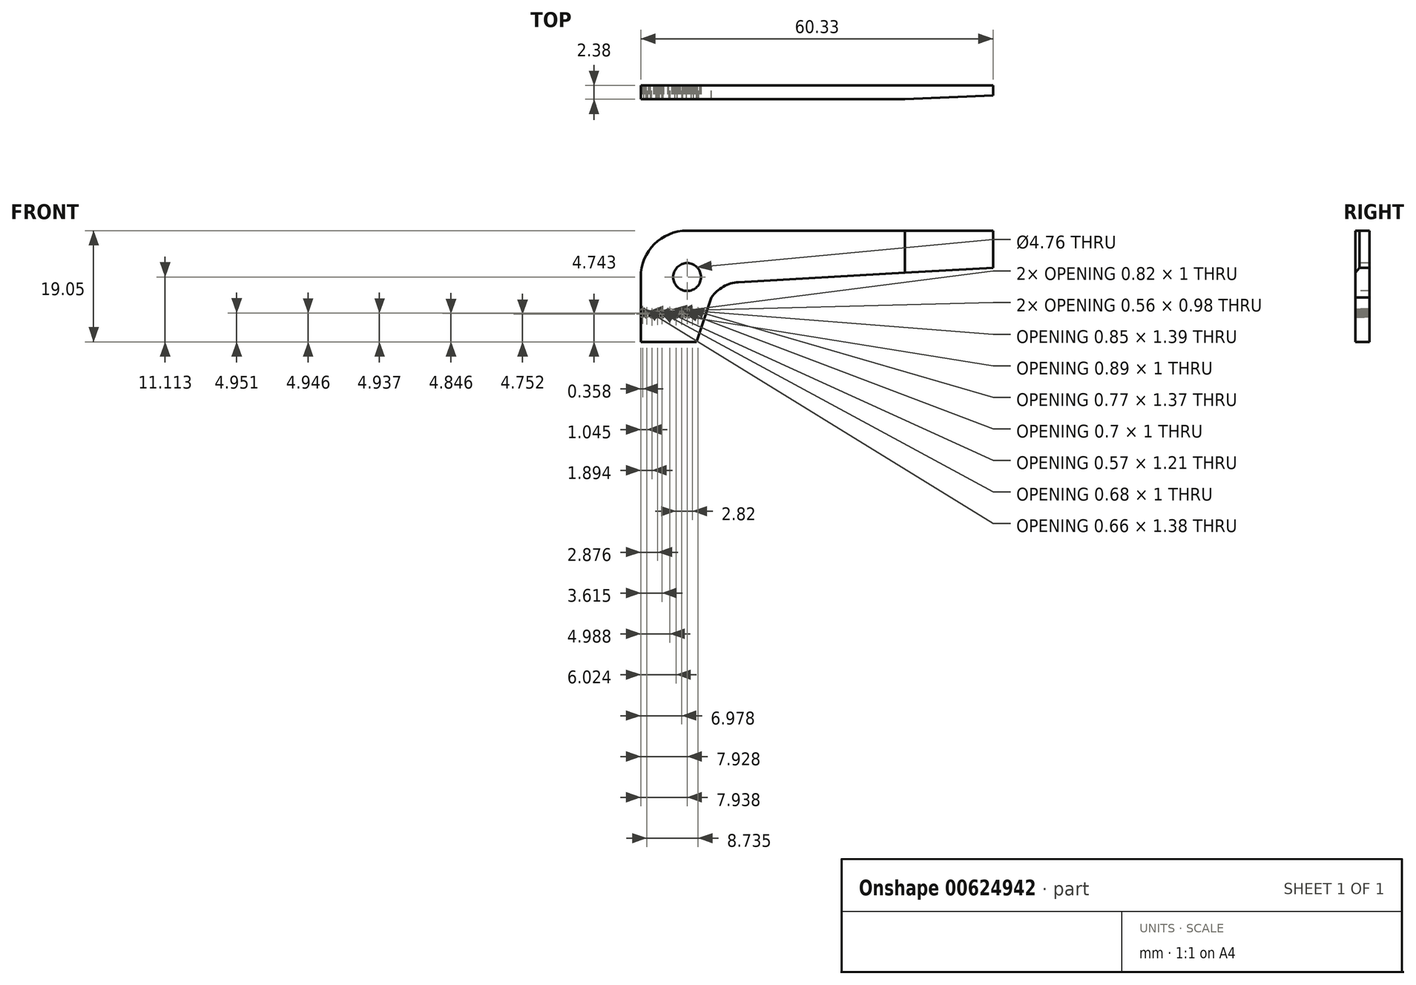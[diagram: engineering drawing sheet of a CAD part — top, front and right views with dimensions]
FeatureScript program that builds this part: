
annotation { "Feature Type Name" : "Feature", "Feature Type Description" : "" }
export const myFeature = defineFeature(function(context is Context, id is Id, definition is map)
    precondition{}
    {
        {
            var Q0;
            Q0=qCreatedBy(makeId("Front.planeOp"),FACE);
            var sketch = newSketch(context, id + "F0", { "sketchPlane" : qUnion([Q0])});
            skLineSegment(sketch, "E0.top", {"start": v(7.94, 19.05) * mm, "end": v(60.33, 19.05) * mm});
            skLineSegment(sketch, "E0.left", {"start": v(0, 0) * mm, "end": v(0, 11.11) * mm});
            skLineSegment(sketch, "E1", {"start": v(9.53, 0) * mm, "end": v(12.11, 7.63) * mm});
            skLineSegment(sketch, "E2", {"start": v(60.33, 12.7) * mm, "end": v(16.75, 10.23) * mm});
            skLineSegment(sketch, "E3", {"start": v(9.53, 0) * mm, "end": v(0, 0) * mm});
            skLineSegment(sketch, "E4", {"start": v(60.33, 12.7) * mm, "end": v(60.33, 19.05) * mm});
            skArc(sketch, "E5", {"start": v(16.75, 10.23) * mm, "mid": v(14.13, 9.46) * mm, "end": v(12.11, 7.63) * mm});
            skPoint(sketch, "E6.visualSharp", {"position": v(0, 19.05) * mm});
            skArc(sketch, "E6.filletArc", {"start": v(7.94, 19.05) * mm, "mid": v(2.32, 16.73) * mm, "end": v(0, 11.11) * mm});
            skSolve(sketch);
        }
        {
            var Q0;
            Q0 = qSketchRegion(id + "F0", true);
            extrude(context, id + "F1", {"entities" : qUnion([Q0]), "depth" : 2.38 * mm, "offsetDistance" : 25.4 * mm});
        }
        {
            var Q0;
            Q0=makeQuery(id+"F1.opExtrude","CAP_FACE",FACE,{"disambiguationData":[OSD([sQuery(id+"F0.wireOp",EDGE,"E0.top"),sQuery(id+"F0.wireOp",EDGE,"E0.left"),sQuery(id+"F0.wireOp",EDGE,"E1"),sQuery(id+"F0.wireOp",EDGE,"E2"),sQuery(id+"F0.wireOp",EDGE,"E3"),sQuery(id+"F0.wireOp",EDGE,"E4"),sQuery(id+"F0.wireOp",EDGE,"E5"),sQuery(id+"F0.wireOp",EDGE,"E6.filletArc")])],"isStart":false});
            var sketch = newSketch(context, id + "F2", { "sketchPlane" : qUnion([Q0])});
            skCircle(sketch, "E7", {"center": v(7.94, 11.11) * mm, "radius": 2.38 * mm});
            skSolve(sketch);
        }
        {
            var Q0;
            Q0=makeQuery(id+"F2.imprint","IMPRINT",FACE,{"disambiguationData":[TD([[makeQuery(id+"F2.imprint","IMPRINT",EDGE,{"derivedFrom":sQuery(id+"F2.wireOp",EDGE,"E7")}),1.0]])]});
            var Q1;
            Q1 = qSketchRegion(id + "F4", true);
            extrude(context, id + "F3", {"entities" : qUnion([Q0, Q1]), "operationType" : NewBodyOperationType.REMOVE, "endBound" : BoundingType.THROUGH_ALL, "oppositeDirection" : true, "depth" : 25.4 * mm, "offsetDistance" : 25.4 * mm});
        }
        {
            var Q0;
            Q0=makeQuery(id+"F1.opExtrude","SWEPT_FACE",FACE,{"disambiguationData":[OSD([sQuery(id+"F0.wireOp",EDGE,"E0.top")])]});
            var sketch = newSketch(context, id + "F4", { "sketchPlane" : qUnion([Q0])});
            skLineSegment(sketch, "E8", {"start": v(45.24, 0) * mm, "end": v(60.33, -0.69) * mm});
            skLineSegment(sketch, "E9", {"start": v(60.33, -0.69) * mm, "end": v(45.24, 0) * mm});
            skLineSegment(sketch, "E10.MirrorCS", {"start": v(60.33, -1.7) * mm, "end": v(45.24, -2.38) * mm});
            skSolve(sketch);
        }
        {
            var Q0;
            {var subQ0=sQuery(id+"F4.wireOp",EDGE,"E10.MirrorCS");Q0=makeQuery(id+"F4.imprint","IMPRINT",FACE,{"disambiguationData":[TD([[makeQuery(id+"F4.imprint","IMPRINT",EDGE,{"derivedFrom":subQ0}),1.0]])]});}
            var Q1;
            {var subQ0=sQuery(id+"F4.wireOp",EDGE,"E9");Q1=makeQuery(id+"F4.imprint","IMPRINT",FACE,{"disambiguationData":[TD([[makeQuery(id+"F4.imprint","IMPRINT",EDGE,{"derivedFrom":subQ0}),-1.0]])]});}
            extrude(context, id + "F5", {"entities" : qUnion([Q0, Q1]), "operationType" : NewBodyOperationType.REMOVE, "oppositeDirection" : true, "depth" : 25.4 * mm, "offsetDistance" : 25.4 * mm});
        }
        {
            var Q0;
            Q0=makeQuery(id+"F1.opExtrude","CAP_FACE",FACE,{"disambiguationData":[OSD([sQuery(id+"F0.wireOp",EDGE,"E0.top"),sQuery(id+"F0.wireOp",EDGE,"E0.left"),sQuery(id+"F0.wireOp",EDGE,"E1"),sQuery(id+"F0.wireOp",EDGE,"E2"),sQuery(id+"F0.wireOp",EDGE,"E3"),sQuery(id+"F0.wireOp",EDGE,"E4"),sQuery(id+"F0.wireOp",EDGE,"E5"),sQuery(id+"F0.wireOp",EDGE,"E6.filletArc")])],"isStart":false});
            var sketch = newSketch(context, id + "F6", { "sketchPlane" : qUnion([Q0])});
            skText(sketch, "E11", { "text": "frost becker", "fontName": "OpenSans-Regular.ttf"});
            const initialGuessF6  = {"E11": [0, 0.00426, 1, 0, 0.0013]};
            skSetInitialGuess(sketch, initialGuessF6);
            skSolve(sketch);
        }
        {
            var Q0;
            Q0 = qSketchRegion(id + "F6", true);
            extrude(context, id + "F7", {"entities" : qUnion([Q0]), "operationType" : NewBodyOperationType.REMOVE, "oppositeDirection" : true, "depth" : 2.54 * mm, "offsetDistance" : 25.4 * mm});
        }
    });
